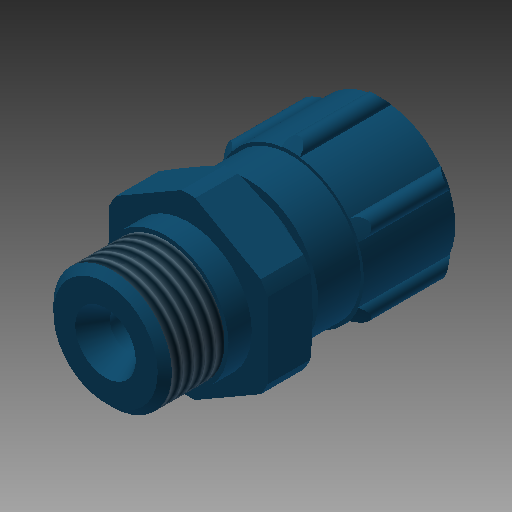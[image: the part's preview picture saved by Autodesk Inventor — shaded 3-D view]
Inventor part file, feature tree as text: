
AUTODESK INVENTOR PART (.ipt)
format: ipt  version: 2018 (Build 220112000, 112)  size: 304,128 bytes
history: native  units: mm
features: other x7, sketch x7, revolve x5, thread x2, extrude x2
ambient origin geometry x8: Origin, YZ Plane, XZ Plane, XY Plane, X Axis, Y Axis, Z Axis, Center Point
bodies: Solid1 (feature_tree)
feature tree (23):
  revolve  "Revolution1"  Angle=360.0deg
  revolve  "Revolution2"  [1 undecoded]
  thread  "Thread1"  [1 undecoded]
  extrude  "Extrusion1"  Depth=4.319mm TaperAngle=0.0deg
  revolve  "Revolution3"  Angle=360.0deg
  revolve  "Revolution4"  [1 undecoded]
  thread  "Thread2"  [1 undecoded]
  extrude  "Extrusion2"  [1 undecoded]
  revolve  "Revolution5"  [1 undecoded]
  other  "ANBAU_XY"
  other  "ANBAU_YZ"
  other  "ANBAU_ZX"
  other  "ANBAU_X"
  other  "ANBAU_Y"
  other  "ANBAU_Z"
  other  "ANBAU_Center"
  sketch  "Sketch_1"  dims[d0=360.0deg d1=360.0deg]
  sketch  "Sketch_2"  dims[d7=360.0deg d8=4.319mm d9=0.0mm]
  sketch  "Sketch_3"  dims[d10=3.7mm d11=0.0mm d12=360.0deg]
  sketch  "Sketch_4"  dims[d13=0.0mm]
  sketch  "Sketch_5"
  sketch  "Sketch_6"
  sketch  "Sketch_7_ALT_Drilling_1"  dims[d2=5.9585mm d3=0.0mm d4=7.5mm d5=0.0mm d6=360.0deg]
note: 6 required parameter values undecoded (feature->parameter linkage not recoverable at this tier; creation-order binding heuristic only, values carry confidence <= 0.55)